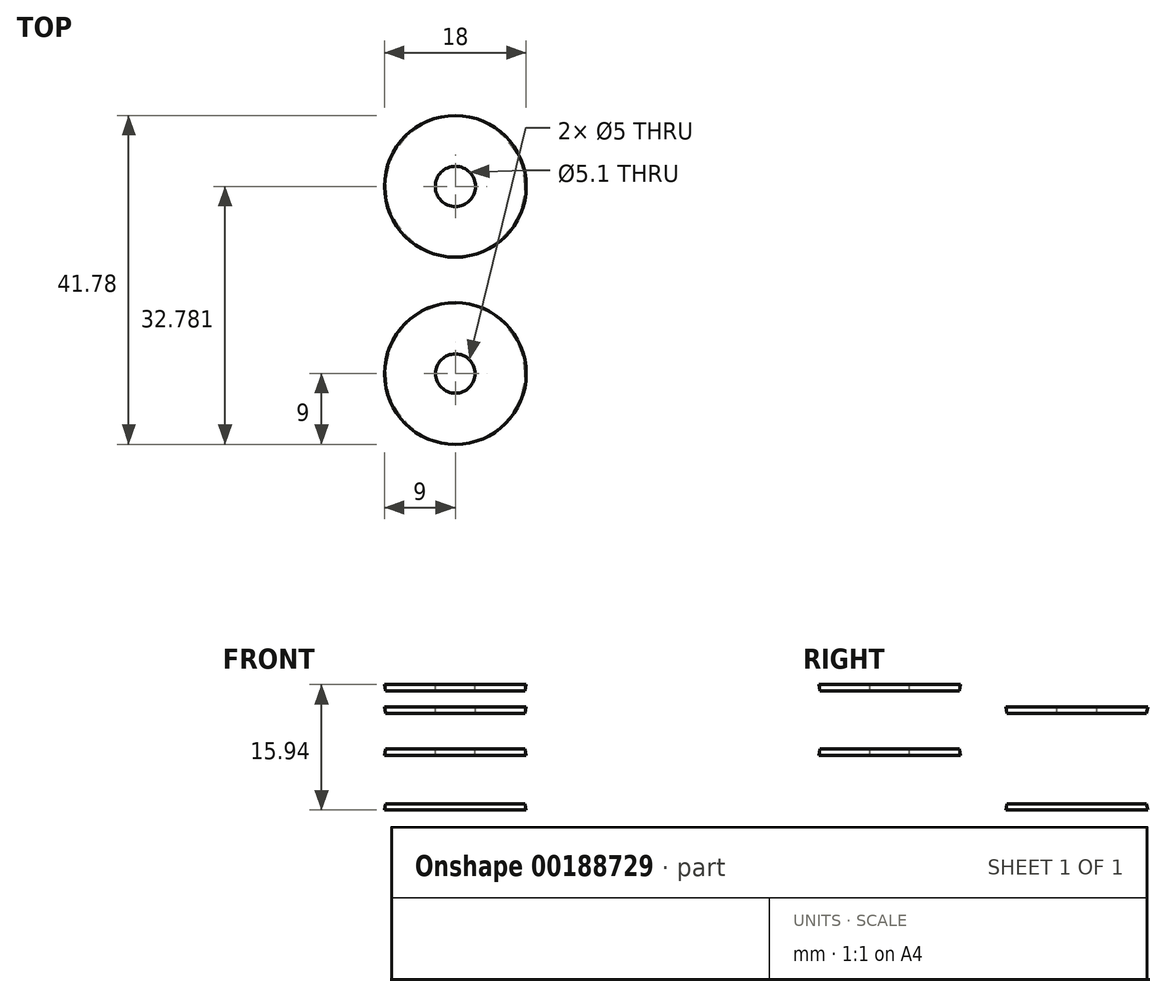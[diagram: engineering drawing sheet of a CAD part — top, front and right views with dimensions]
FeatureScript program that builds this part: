
annotation { "Feature Type Name" : "Feature", "Feature Type Description" : "" }
export const myFeature = defineFeature(function(context is Context, id is Id, definition is map)
    precondition{}
    {
        {
            var Q0;
            Q0=qCreatedBy(makeId("Front.planeOp"),FACE);
            var sketch = newSketch(context, id + "F0", { "sketchPlane" : qUnion([Q0])});
            skLineSegment(sketch, "E0", {"start": v(0, -26.92) * mm, "end": v(0, 33.9) * mm, "construction": true});
            skLineSegment(sketch, "E1", {"start": v(-9, 11.69) * mm, "end": v(0, 11.69) * mm});
            skLineSegment(sketch, "E2", {"start": v(0, 11.69) * mm, "end": v(0, 10.89) * mm});
            skLineSegment(sketch, "E3", {"start": v(0, 10.89) * mm, "end": v(-8.86, 10.89) * mm});
            skLineSegment(sketch, "E4", {"start": v(-8.86, 10.89) * mm, "end": v(-9, 11.69) * mm});
            skLineSegment(sketch, "E5.bottom", {"start": v(0, 10.89) * mm, "end": v(-6, 10.89) * mm});
            skLineSegment(sketch, "E5.top", {"start": v(0, 3.49) * mm, "end": v(-6, 3.49) * mm});
            skLineSegment(sketch, "E5.left", {"start": v(0, 10.89) * mm, "end": v(0, 3.49) * mm});
            skLineSegment(sketch, "E5.right", {"start": v(-6, 10.89) * mm, "end": v(-6, 3.49) * mm});
            skLineSegment(sketch, "E6", {"start": v(-8.86, 3.49) * mm, "end": v(0, 3.49) * mm});
            skLineSegment(sketch, "E7", {"start": v(0, 2.69) * mm, "end": v(-9, 2.69) * mm});
            skLineSegment(sketch, "E8", {"start": v(-9, 2.69) * mm, "end": v(-8.86, 3.49) * mm});
            skLineSegment(sketch, "E9", {"start": v(0, 3.49) * mm, "end": v(0, 2.69) * mm});
            skLineSegment(sketch, "E10", {"start": v(-8.86, 10.89) * mm, "end": v(-9, 10.89) * mm, "construction": true});
            skLineSegment(sketch, "E11", {"start": v(-8.86, 3.49) * mm, "end": v(-9, 3.49) * mm, "construction": true});
            skSolve(sketch);
        }
        {
            var Q0;
            Q0=makeQuery(id+"F0.imprint","IMPRINT",FACE,{"disambiguationData":[TD([[makeQuery(id+"F0.imprint","IMPRINT",EDGE,{"derivedFrom":sQuery(id+"F0.wireOp",EDGE,"E1")}),-1.0]])]});
            var Q1;
            Q1=makeQuery(id+"F0.imprint","IMPRINT",FACE,{"disambiguationData":[TD([[makeQuery(id+"F0.imprint","IMPRINT",EDGE,{"derivedFrom":sQuery(id+"F0.wireOp",EDGE,"E5.bottom")}),1.0]])]});
            var Q2;
            Q2=makeQuery(id+"F0.imprint","IMPRINT",FACE,{"disambiguationData":[TD([[makeQuery(id+"F0.imprint","IMPRINT",EDGE,{"derivedFrom":sQuery(id+"F0.wireOp",EDGE,"E7")}),-1.0]])]});
            var Q3;
            Q3=sQuery(id+"F0.wireOp",EDGE,"E0");
            revolve(context, id + "F1", {"entities" : qUnion([Q0, Q1, Q2]), "axis" : qUnion([Q3]), "revolveType" : RevolveType.FULL});
        }
        {
            var Q0;
            Q0=makeQuery(id+"F1.opRevolve","SWEPT_FACE",FACE,{"disambiguationData":[OSD([sQuery(id+"F0.wireOp",EDGE,"E1")])]});
            var sketch = newSketch(context, id + "F2", { "sketchPlane" : qUnion([Q0])});
            skCircle(sketch, "E12", {"center": v(0, 0) * mm, "radius": 2.5 * mm});
            skSolve(sketch);
        }
        {
            var Q0;
            Q0=makeQuery(id+"F2.imprint","IMPRINT",FACE,{"disambiguationData":[TD([[makeQuery(id+"F2.imprint","IMPRINT",EDGE,{"derivedFrom":sQuery(id+"F2.wireOp",EDGE,"E12")}),1.0]])]});
            var Q1;
            Q1=sQuery(id+"F2.wireOp",EDGE,"E12");
            var Q2;
            Q2=makeQuery(id+"F1.opRevolve","SWEPT_FACE",FACE,{"disambiguationData":[OSD([sQuery(id+"F0.wireOp",EDGE,"E7")])]});
            extrude(context, id + "F3", {"entities" : qUnion([Q0]), "operationType" : NewBodyOperationType.REMOVE, "surfaceEntities" : qUnion([Q1]), "endBound" : BoundingType.UP_TO_SURFACE, "oppositeDirection" : true, "endBoundEntityFace" : qUnion([Q2]), "depth" : 25 * mm});
        }
        {
            var Q0;
            Q0=qCreatedBy(makeId("Right.planeOp"),FACE);
            var sketch = newSketch(context, id + "F4", { "sketchPlane" : qUnion([Q0])});
            skLineSegment(sketch, "E13", {"start": v(23.78, -33.86) * mm, "end": v(23.78, 26.95) * mm, "construction": true});
            skLineSegment(sketch, "E14", {"start": v(14.78, 8.85) * mm, "end": v(23.78, 8.85) * mm});
            skLineSegment(sketch, "E15", {"start": v(23.78, 8.85) * mm, "end": v(23.78, 8.05) * mm});
            skLineSegment(sketch, "E16", {"start": v(23.78, 8.05) * mm, "end": v(14.92, 8.05) * mm});
            skLineSegment(sketch, "E17", {"start": v(14.92, 8.05) * mm, "end": v(14.78, 8.85) * mm});
            skLineSegment(sketch, "E18.bottom", {"start": v(23.78, 8.05) * mm, "end": v(17.73, 8.05) * mm});
            skLineSegment(sketch, "E18.top", {"start": v(23.78, -3.45) * mm, "end": v(17.73, -3.45) * mm});
            skLineSegment(sketch, "E18.left", {"start": v(23.78, 8.05) * mm, "end": v(23.78, -3.45) * mm});
            skLineSegment(sketch, "E18.right", {"start": v(17.73, 8.05) * mm, "end": v(17.73, -3.45) * mm});
            skLineSegment(sketch, "E19", {"start": v(14.92, -3.45) * mm, "end": v(23.78, -3.45) * mm});
            skLineSegment(sketch, "E20", {"start": v(23.78, -4.25) * mm, "end": v(14.78, -4.25) * mm});
            skLineSegment(sketch, "E21", {"start": v(14.78, -4.25) * mm, "end": v(14.92, -3.45) * mm});
            skLineSegment(sketch, "E22", {"start": v(23.78, -3.45) * mm, "end": v(23.78, -4.25) * mm});
            skLineSegment(sketch, "E23", {"start": v(14.92, 8.05) * mm, "end": v(14.78, 8.05) * mm, "construction": true});
            skLineSegment(sketch, "E24", {"start": v(14.92, -3.45) * mm, "end": v(14.78, -3.45) * mm, "construction": true});
            skSolve(sketch);
        }
        {
            var Q0;
            Q0=makeQuery(id+"F4.imprint","IMPRINT",FACE,{"disambiguationData":[TD([[makeQuery(id+"F4.imprint","IMPRINT",EDGE,{"derivedFrom":sQuery(id+"F4.wireOp",EDGE,"E20")}),-1.0]])]});
            var Q1;
            Q1=makeQuery(id+"F4.imprint","IMPRINT",FACE,{"disambiguationData":[TD([[makeQuery(id+"F4.imprint","IMPRINT",EDGE,{"derivedFrom":sQuery(id+"F4.wireOp",EDGE,"E18.bottom")}),1.0]])]});
            var Q2;
            Q2=makeQuery(id+"F4.imprint","IMPRINT",FACE,{"disambiguationData":[TD([[makeQuery(id+"F4.imprint","IMPRINT",EDGE,{"derivedFrom":sQuery(id+"F4.wireOp",EDGE,"E14")}),-1.0]])]});
            var Q3;
            Q3=sQuery(id+"F4.wireOp",EDGE,"E13");
            revolve(context, id + "F5", {"entities" : qUnion([Q0, Q1, Q2]), "axis" : qUnion([Q3]), "revolveType" : RevolveType.FULL});
        }
        {
            var Q0;
            Q0=makeQuery(id+"F5.opRevolve","SWEPT_FACE",FACE,{"disambiguationData":[OSD([sQuery(id+"F4.wireOp",EDGE,"E14")])]});
            var sketch = newSketch(context, id + "F6", { "sketchPlane" : qUnion([Q0])});
            skCircle(sketch, "E25", {"center": v(0, 23.78) * mm, "radius": 2.55 * mm});
            skSolve(sketch);
        }
        {
            var Q0;
            Q0=makeQuery(id+"F6.imprint","IMPRINT",FACE,{"disambiguationData":[TD([[makeQuery(id+"F6.imprint","IMPRINT",EDGE,{"derivedFrom":sQuery(id+"F6.wireOp",EDGE,"E25")}),1.0]])]});
            extrude(context, id + "F7", {"entities" : qUnion([Q0]), "operationType" : NewBodyOperationType.REMOVE, "endBound" : BoundingType.UP_TO_NEXT, "oppositeDirection" : true, "depth" : 25 * mm});
        }
    });
